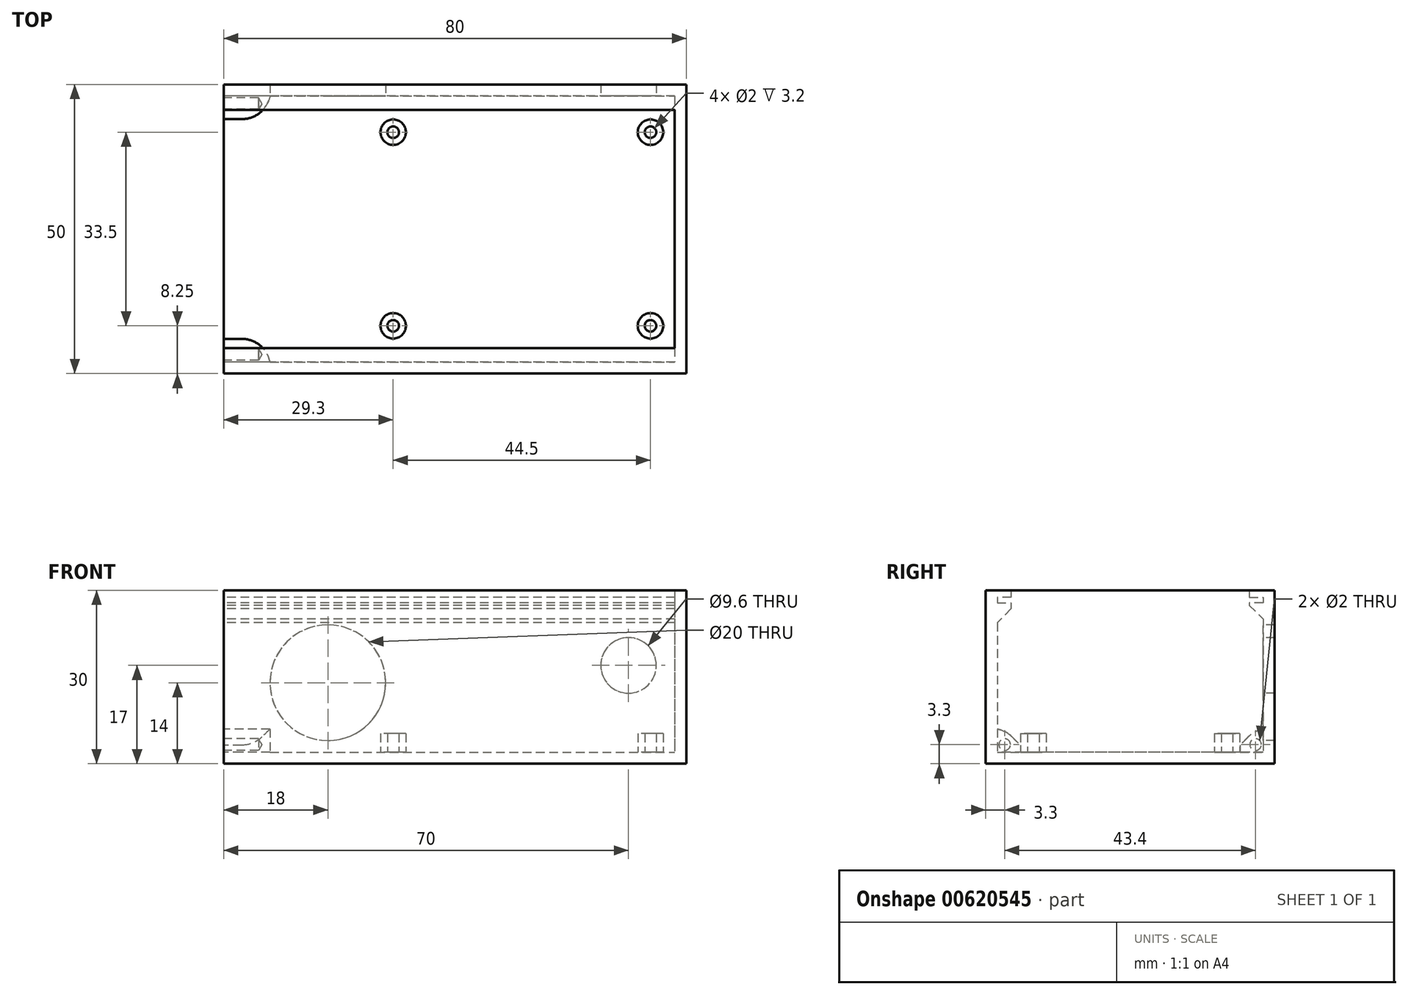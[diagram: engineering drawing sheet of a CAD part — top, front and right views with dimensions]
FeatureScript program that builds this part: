
annotation { "Feature Type Name" : "Feature", "Feature Type Description" : "" }
export const myFeature = defineFeature(function(context is Context, id is Id, definition is map)
    precondition{}
    {
        {
            var Q0;
            Q0=qCreatedBy(makeId("Top.planeOp"),FACE);
            var sketch = newSketch(context, id + "F0", { "sketchPlane" : qUnion([Q0])});
            skLineSegment(sketch, "E0.bottom", {"start": v(-40, 25) * mm, "end": v(40, 25) * mm});
            skLineSegment(sketch, "E0.top", {"start": v(-40, -25) * mm, "end": v(40, -25) * mm});
            skLineSegment(sketch, "E0.left", {"start": v(-40, 25) * mm, "end": v(-40, -25) * mm});
            skLineSegment(sketch, "E0.right", {"start": v(40, 25) * mm, "end": v(40, -25) * mm});
            skLineSegment(sketch, "E1", {"start": v(-40, 25) * mm, "end": v(40, -25) * mm, "construction": true});
            skSolve(sketch);
        }
        {
            var Q0;
            Q0 = qSketchRegion(id + "F0", true);
            extrude(context, id + "F1", {"entities" : qUnion([Q0]), "depth" : 30 * mm, "offsetDistance" : 25 * mm});
        }
        {
            var Q0;
            Q0=makeQuery(id+"F1.opExtrude","CAP_FACE",FACE,{"disambiguationData":[OSD([sQuery(id+"F0.wireOp",EDGE,"E0.bottom"),sQuery(id+"F0.wireOp",EDGE,"E0.top"),sQuery(id+"F0.wireOp",EDGE,"E0.left"),sQuery(id+"F0.wireOp",EDGE,"E0.right")])],"isStart":false});
            shell(context, id + "F2", {"entities" : qUnion([Q0]), "thickness" : 2 * mm});
        }
        {
            var Q0;
            Q0=makeQuery(id+"F0.imprint","IMPRINT",FACE,{"disambiguationData":[TD([[makeQuery(id+"F0.imprint","IMPRINT",EDGE,{"derivedFrom":sQuery(id+"F0.wireOp",EDGE,"E0.bottom")}),-1.0]])]});
            var sketch = newSketch(context, id + "F3", { "sketchPlane" : qUnion([Q0])});
            skCircle(sketch, "E2", {"center": v(-10.7, 16.75) * mm, "radius": 1 * mm});
            skCircle(sketch, "E3", {"center": v(33.8, 16.75) * mm, "radius": 1 * mm});
            skCircle(sketch, "E4", {"center": v(33.8, -16.75) * mm, "radius": 1 * mm});
            skCircle(sketch, "E5", {"center": v(-10.7, -16.75) * mm, "radius": 1 * mm});
            skLineSegment(sketch, "E6.bottom", {"start": v(-10.7, 16.75) * mm, "end": v(33.8, 16.75) * mm, "construction": true});
            skLineSegment(sketch, "E6.top", {"start": v(-10.7, -16.75) * mm, "end": v(33.8, -16.75) * mm, "construction": true});
            skLineSegment(sketch, "E6.left", {"start": v(-10.7, 16.75) * mm, "end": v(-10.7, -16.75) * mm, "construction": true});
            skLineSegment(sketch, "E6.right", {"start": v(33.8, 16.75) * mm, "end": v(33.8, -16.75) * mm, "construction": true});
            skLineSegment(sketch, "E7", {"start": v(40, 0) * mm, "end": v(-40, 0) * mm, "construction": true});
            skLineSegment(sketch, "E8", {"start": v(-10.7, 0) * mm, "end": v(33.8, 0) * mm, "construction": true});
            skCircle(sketch, "E9.0", {"center": v(-10.7, 16.75) * mm, "radius": 2.2 * mm});
            skCircle(sketch, "E10.0", {"center": v(-10.7, -16.75) * mm, "radius": 2.2 * mm});
            skCircle(sketch, "E11.0", {"center": v(33.8, 16.75) * mm, "radius": 2.2 * mm});
            skCircle(sketch, "E12.0", {"center": v(33.8, -16.75) * mm, "radius": 2.2 * mm});
            skSolve(sketch);
        }
        {
            var Q0;
            Q0 = qSketchRegion(id + "F3", true);
            extrude(context, id + "F4", {"entities" : qUnion([Q0]), "operationType" : NewBodyOperationType.ADD, "depth" : 5.2 * mm, "offsetDistance" : 25 * mm});
        }
        {
            var Q0;
            Q0=makeQuery(id+"F2.opShell","OFFSET_FACE",FACE,{"disambiguationData":[OSD([sQuery(id+"F0.wireOp",EDGE,"E0.left")])]});
            var sketch = newSketch(context, id + "F5", { "sketchPlane" : qUnion([Q0])});
            skLineSegment(sketch, "E13", {"start": v(23, 30) * mm, "end": v(23, 2) * mm});
            skLineSegment(sketch, "E14", {"start": v(23, 2) * mm, "end": v(-23, 2) * mm});
            skLineSegment(sketch, "E15", {"start": v(-23, 2) * mm, "end": v(-23, 30) * mm});
            skLineSegment(sketch, "E16", {"start": v(-23, 30) * mm, "end": v(23, 30) * mm});
            skSolve(sketch);
        }
        {
            var Q0;
            Q0 = qSketchRegion(id + "F5", true);
            extrude(context, id + "F6", {"entities" : qUnion([Q0]), "operationType" : NewBodyOperationType.REMOVE, "oppositeDirection" : true, "depth" : 25 * mm, "offsetDistance" : 25 * mm});
        }
        {
            var Q0;
            Q0=makeQuery(id+"F1.opExtrude","SWEPT_FACE",FACE,{"disambiguationData":[OSD([sQuery(id+"F0.wireOp",EDGE,"E0.left")])]});
            var sketch = newSketch(context, id + "F7", { "sketchPlane" : qUnion([Q0])});
            skLineSegment(sketch, "E17", {"start": v(-23, 30) * mm, "end": v(-20.6, 30) * mm});
            skLineSegment(sketch, "E18", {"start": v(-20.6, 30) * mm, "end": v(-20.6, 28.8) * mm});
            skLineSegment(sketch, "E19", {"start": v(-20.6, 28.8) * mm, "end": v(-23, 28.8) * mm});
            skLineSegment(sketch, "E20", {"start": v(-23, 28.8) * mm, "end": v(-23, 27.8) * mm});
            skLineSegment(sketch, "E21", {"start": v(-23, 27.8) * mm, "end": v(-20.6, 27.8) * mm});
            skLineSegment(sketch, "E22", {"start": v(-20.6, 27.8) * mm, "end": v(-20.6, 27.4) * mm});
            skLineSegment(sketch, "E23", {"start": v(-20.6, 27.4) * mm, "end": v(-23, 25) * mm});
            skLineSegment(sketch, "E24", {"start": v(-23, 25) * mm, "end": v(-23, 27.8) * mm});
            skLineSegment(sketch, "E25", {"start": v(23, 30) * mm, "end": v(20.6, 30) * mm});
            skLineSegment(sketch, "E26.MirrorCS", {"start": v(20.6, 30) * mm, "end": v(20.6, 28.8) * mm});
            skLineSegment(sketch, "E27.MirrorCS", {"start": v(20.6, 28.8) * mm, "end": v(23, 28.8) * mm});
            skLineSegment(sketch, "E28.MirrorCS", {"start": v(23, 28.8) * mm, "end": v(23, 27.8) * mm});
            skLineSegment(sketch, "E29.MirrorCS", {"start": v(23, 27.8) * mm, "end": v(20.6, 27.8) * mm});
            skLineSegment(sketch, "E30.MirrorCS", {"start": v(20.6, 27.8) * mm, "end": v(20.6, 26.8) * mm});
            skLineSegment(sketch, "E31.MirrorCS", {"start": v(20.6, 26.8) * mm, "end": v(23, 24.4) * mm});
            skSolve(sketch);
        }
        {
            var Q0;
            Q0 = qSketchRegion(id + "F7", true);
            var Q1;
            {var subQ0=sQuery(id+"F7.wireOp",EDGE,"E29.MirrorCS");Q1=makeQuery(id+"F7.imprint","IMPRINT",FACE,{"disambiguationData":[TD([[makeQuery(id+"F7.imprint","IMPRINT",EDGE,{"derivedFrom":subQ0}),1.0]])]});}
            var Q2;
            {var subQ0=sQuery(id+"F7.wireOp",EDGE,"E25");Q2=makeQuery(id+"F7.imprint","IMPRINT",FACE,{"disambiguationData":[TD([[makeQuery(id+"F7.imprint","IMPRINT",EDGE,{"derivedFrom":subQ0}),1.0]])]});}
            var Q3;
            {var subQ0=sQuery(id+"F7.wireOp",EDGE,"E17");Q3=makeQuery(id+"F7.imprint","IMPRINT",FACE,{"disambiguationData":[TD([[makeQuery(id+"F7.imprint","IMPRINT",EDGE,{"derivedFrom":subQ0}),-1.0]])]});}
            extrude(context, id + "F8", {"entities" : qUnion([Q0, Q1, Q2, Q3]), "operationType" : NewBodyOperationType.ADD, "endBound" : BoundingType.UP_TO_NEXT, "oppositeDirection" : true, "depth" : 25 * mm, "offsetDistance" : 25 * mm});
        }
        {
            var Q0;
            {var subQ0=sQuery(id+"F5.wireOp",EDGE,"E15");var subQ1=sQuery(id+"F0.wireOp",EDGE,"E0.left");Q0=makeQuery(id+"F8.boolean.opBoolean","MERGE",FACE,{"derivedFrom":[makeQuery(id+"F1.opExtrude","SWEPT_FACE",FACE,{"disambiguationData":[OSD([subQ1])]}),makeQuery(id+"F8.opExtrude","CAP_FACE",FACE,{"disambiguationData":[OSD([subQ1,sQuery(id+"F5.wireOp",EDGE,"E13"),sQuery(id+"F7.wireOp",EDGE,"E17"),sQuery(id+"F7.wireOp",EDGE,"E18"),sQuery(id+"F7.wireOp",EDGE,"E19")])],"isStart":true}),makeQuery(id+"F8.opExtrude","CAP_FACE",FACE,{"disambiguationData":[OSD([sQuery(id+"F7.wireOp",EDGE,"E21"),sQuery(id+"F7.wireOp",EDGE,"E22"),sQuery(id+"F7.wireOp",EDGE,"E23"),sQuery(id+"F7.wireOp",EDGE,"E24")])],"isStart":true}),makeQuery(id+"F8.opExtrude","CAP_FACE",FACE,{"disambiguationData":[OSD([subQ1,subQ0,sQuery(id+"F7.wireOp",EDGE,"E25"),sQuery(id+"F7.wireOp",EDGE,"E26.MirrorCS"),sQuery(id+"F7.wireOp",EDGE,"E27.MirrorCS")])],"isStart":true}),makeQuery(id+"F8.opExtrude","CAP_FACE",FACE,{"disambiguationData":[OSD([subQ1,subQ0,sQuery(id+"F7.wireOp",EDGE,"E29.MirrorCS"),sQuery(id+"F7.wireOp",EDGE,"E30.MirrorCS"),sQuery(id+"F7.wireOp",EDGE,"E31.MirrorCS")])],"isStart":true})]});}
            var sketch = newSketch(context, id + "F9", { "sketchPlane" : qUnion([Q0])});
            skLineSegment(sketch, "E32", {"start": v(-23, 2) * mm, "end": v(-23, 6) * mm});
            skLineSegment(sketch, "E33", {"start": v(-23, 6) * mm, "end": v(-21.8, 6) * mm});
            skLineSegment(sketch, "E34", {"start": v(-21.8, 6) * mm, "end": v(-19, 3.2) * mm});
            skLineSegment(sketch, "E35", {"start": v(-19, 3.2) * mm, "end": v(-19, 2) * mm});
            skLineSegment(sketch, "E36", {"start": v(-19, 2) * mm, "end": v(-23, 2) * mm});
            skLineSegment(sketch, "E37", {"start": v(-23, 2) * mm, "end": v(-20.4, 4.6) * mm});
            skLineSegment(sketch, "E38", {"start": v(23, 2) * mm, "end": v(23, 6) * mm});
            skLineSegment(sketch, "E39", {"start": v(23, 6) * mm, "end": v(21.8, 6) * mm});
            skLineSegment(sketch, "E40", {"start": v(21.8, 6) * mm, "end": v(19, 3.2) * mm});
            skLineSegment(sketch, "E41", {"start": v(19, 3.2) * mm, "end": v(19, 2) * mm});
            skLineSegment(sketch, "E42", {"start": v(23, 2) * mm, "end": v(19, 2) * mm});
            skLineSegment(sketch, "E43", {"start": v(23, 2) * mm, "end": v(20.4, 4.6) * mm, "construction": true});
            skLineSegment(sketch, "E44", {"start": v(-21.7, 3.3) * mm, "end": v(-20.4, 4.6) * mm});
            skLineSegment(sketch, "E45", {"start": v(21.7, 3.3) * mm, "end": v(20.4, 2) * mm, "construction": true});
            skSolve(sketch);
        }
        {
            var Q0;
            Q0 = qSketchRegion(id + "F9", true);
            extrude(context, id + "F10", {"entities" : qUnion([Q0]), "operationType" : NewBodyOperationType.ADD, "oppositeDirection" : true, "depth" : 8 * mm, "offsetDistance" : 25 * mm});
        }
        {
            var Q0;
            Q0=makeQuery(id+"F10.opExtrude","CAP_EDGE",EDGE,{"disambiguationData":[OSD([sQuery(id+"F9.wireOp",EDGE,"E35")])],"isStart":false});
            var Q1;
            Q1=makeQuery(id+"F10.opExtrude","CAP_EDGE",EDGE,{"disambiguationData":[OSD([sQuery(id+"F9.wireOp",EDGE,"E41")])],"isStart":false});
            var Q2;
            Q2=makeQuery(id+"F10.opExtrude","SWEPT_EDGE",EDGE,{"disambiguationData":[OSD([sQuery(id+"F9.wireOp",EDGE,"E39"),sQuery(id+"F9.wireOp",EDGE,"E40")])]});
            var Q3;
            Q3=makeQuery(id+"F10.opExtrude","SWEPT_EDGE",EDGE,{"disambiguationData":[OSD([sQuery(id+"F9.wireOp",EDGE,"E33"),sQuery(id+"F9.wireOp",EDGE,"E34")])]});
            fillet(context, id + "F11", {"entities" : qUnion([Q0, Q1, Q2, Q3]), "radius" : 5 * mm, "tangentPropagation" : true, "allowEdgeOverflow" : false});
        }
        {
            var Q0;
            Q0=sQuery(id+"F9.wireOp",VERTEX,"E44.start");
            var Q1;
            Q1=sQuery(id+"F9.wireOp",VERTEX,"E45.start");
            var Q2;
            Q2=makeQuery(id+"F1.opExtrude","SWEPT_BODY",BODY,{"disambiguationData":[OSD([sQuery(id+"F0.wireOp",EDGE,"E0.bottom"),sQuery(id+"F0.wireOp",EDGE,"E0.top"),sQuery(id+"F0.wireOp",EDGE,"E0.left"),sQuery(id+"F0.wireOp",EDGE,"E0.right")])]});
            hole(context, id + "F12", {"style" : HoleStyle.SIMPLE, "endStyle" : HoleEndStyle.BLIND, "holeDiameter" : 2 * mm, "majorDiameter" : 5 * mm, "holeDepth" : 6 * mm, "isTappedThrough" : true, "tappedDepth" : 12 * mm, "tapClearance" : 3, "locations" : qUnion([Q0, Q1]), "scope" : qUnion([Q2])});
        }
        {
            var Q0;
            {var subQ0=sQuery(id+"F5.wireOp",EDGE,"E13");var subQ4=sQuery(id+"F0.wireOp",EDGE,"E0.bottom");var subQ5=sQuery(id+"F7.wireOp",EDGE,"E23");Q0=makeQuery(id+"F8.boolean.opBoolean","SPLIT",FACE,{"disambiguationData":[TD([makeQuery(id+"F8.opExtrude","SWEPT_FACE",FACE,{"disambiguationData":[OSD([subQ5])]})])],"derivedFrom":makeQuery(id+"F6.boolean.opBoolean","MERGE",FACE,{"derivedFrom":[makeQuery(id+"F2.opShell","OFFSET_FACE",FACE,{"disambiguationData":[OSD([subQ4])]})],"fromTools":[makeQuery(id+"F6.opExtrude","SWEPT_FACE",FACE,{"disambiguationData":[OSD([subQ0])]})]})});}
            var sketch = newSketch(context, id + "F13", { "sketchPlane" : qUnion([Q0])});
            skLineSegment(sketch, "E46", {"start": v(-22, 2) * mm, "end": v(-22, 25) * mm, "construction": true});
            skLineSegment(sketch, "E47", {"start": v(-40, 14) * mm, "end": v(-22, 14) * mm, "construction": true});
            skCircle(sketch, "E48", {"center": v(-22, 14) * mm, "radius": 10 * mm});
            skLineSegment(sketch, "E49", {"start": v(30, 2) * mm, "end": v(30, 25) * mm});
            skLineSegment(sketch, "E50", {"start": v(30, 17) * mm, "end": v(38, 17) * mm});
            skCircle(sketch, "E51", {"center": v(30, 17) * mm, "radius": 4.8 * mm});
            skSolve(sketch);
        }
        {
            var Q0;
            Q0=makeQuery(id+"F13.imprint","IMPRINT",FACE,{"disambiguationData":[TD([[makeQuery(id+"F13.imprint","IMPRINT",EDGE,{"derivedFrom":sQuery(id+"F13.wireOp",EDGE,"E48")}),1.0]])]});
            var Q1;
            {var subQ0=sQuery(id+"F13.wireOp",EDGE,"E49");var subQ1=makeQuery(id+"F13.imprint","INTERSECT",VERTEX,{"derivedFrom":[subQ0,sQuery(id+"F13.wireOp",EDGE,"E50")]});Q1=makeQuery(id+"F13.imprint","IMPRINT",FACE,{"disambiguationData":[TD([[makeQuery(id+"F13.imprint","IMPRINT",EDGE,{"disambiguationData":[TD([[subQ1,1.0]])],"derivedFrom":subQ0}),1.0]])]});}
            var Q2;
            {var subQ0=sQuery(id+"F13.wireOp",EDGE,"E50");var subQ1=sQuery(id+"F13.wireOp",EDGE,"E49");var subQ2=makeQuery(id+"F13.imprint","INTERSECT",VERTEX,{"derivedFrom":[subQ1,subQ0]});Q2=makeQuery(id+"F13.imprint","IMPRINT",FACE,{"disambiguationData":[TD([[makeQuery(id+"F13.imprint","IMPRINT",EDGE,{"disambiguationData":[TD([[subQ2,-1.0]])],"derivedFrom":subQ1}),-1.0]])]});}
            var Q3;
            {var subQ0=sQuery(id+"F13.wireOp",EDGE,"E50");var subQ1=sQuery(id+"F13.wireOp",EDGE,"E49");var subQ2=makeQuery(id+"F13.imprint","INTERSECT",VERTEX,{"derivedFrom":[subQ1,subQ0]});Q3=makeQuery(id+"F13.imprint","IMPRINT",FACE,{"disambiguationData":[TD([[makeQuery(id+"F13.imprint","IMPRINT",EDGE,{"disambiguationData":[TD([[subQ2,1.0]])],"derivedFrom":subQ1}),-1.0]])]});}
            extrude(context, id + "F14", {"entities" : qUnion([Q0, Q1, Q2, Q3]), "operationType" : NewBodyOperationType.REMOVE, "oppositeDirection" : true, "depth" : 25 * mm, "offsetDistance" : 25 * mm});
        }
    });
